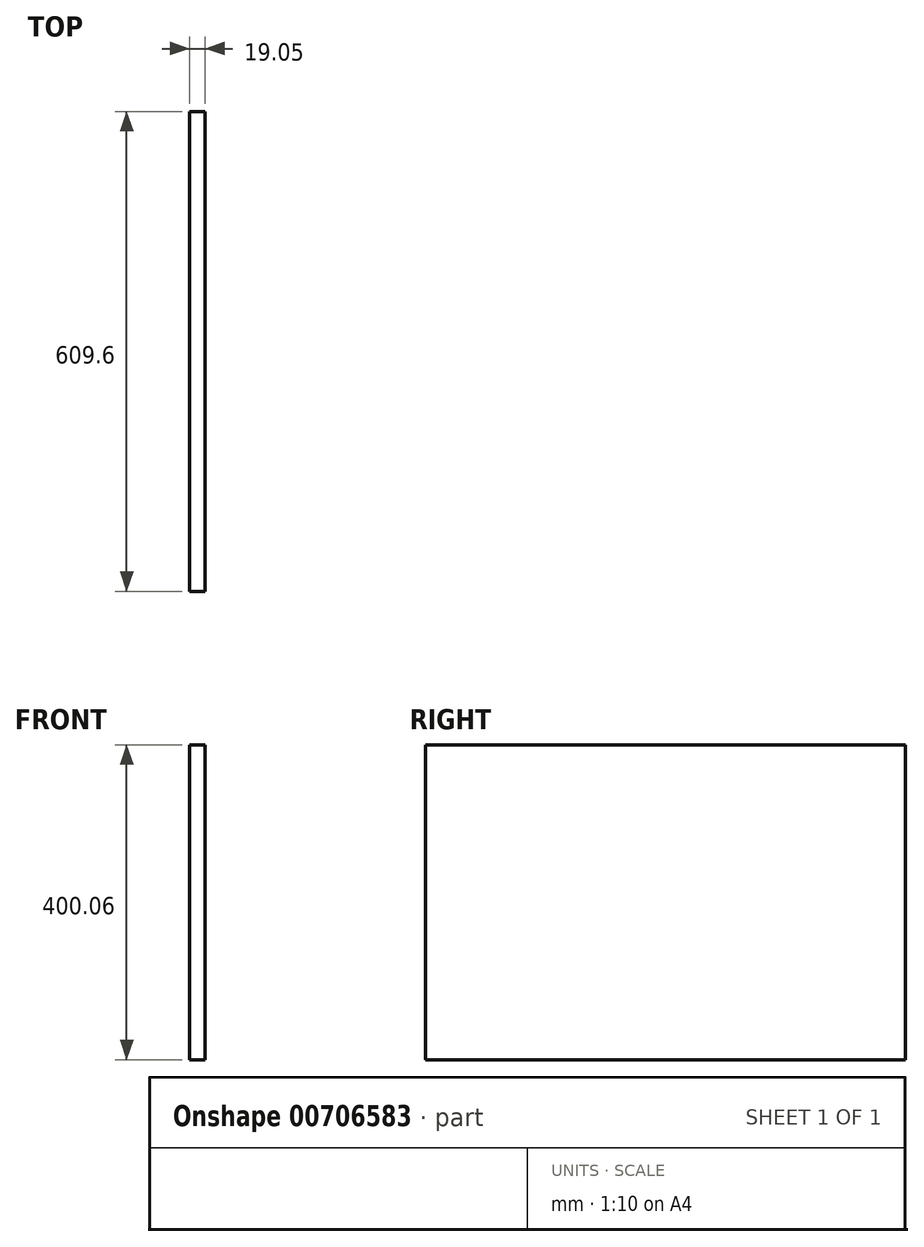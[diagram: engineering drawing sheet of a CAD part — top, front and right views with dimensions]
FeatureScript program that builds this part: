
annotation { "Feature Type Name" : "Feature", "Feature Type Description" : "" }
export const myFeature = defineFeature(function(context is Context, id is Id, definition is map)
    precondition{}
    {
        {
            var Q0;
            Q0=qCreatedBy(makeId("Right.planeOp"),FACE);
            var sketch = newSketch(context, id + "F0", { "sketchPlane" : qUnion([Q0])});
            skLineSegment(sketch, "E0.bottom", {"start": v(304.8, 200.03) * mm, "end": v(-304.8, 200.03) * mm});
            skLineSegment(sketch, "E0.top", {"start": v(304.8, -200.03) * mm, "end": v(-304.8, -200.03) * mm});
            skLineSegment(sketch, "E0.left", {"start": v(304.8, 200.02) * mm, "end": v(304.8, -200.03) * mm});
            skLineSegment(sketch, "E0.right", {"start": v(-304.8, 200.03) * mm, "end": v(-304.8, -200.03) * mm});
            skPoint(sketch, "E0.middle", {"position": v(0, 0) * mm});
            skSolve(sketch);
        }
        {
            var Q0;
            Q0=makeQuery(id+"F0.imprint","IMPRINT",FACE,{"disambiguationData":[TD([[makeQuery(id+"F0.imprint","IMPRINT",EDGE,{"derivedFrom":sQuery(id+"F0.wireOp",EDGE,"E0.bottom")}),1.0]])]});
            extrude(context, id + "F1", {"entities" : qUnion([Q0]), "depth" : 19.05 * mm, "offsetDistance" : 25.4 * mm});
        }
    });
